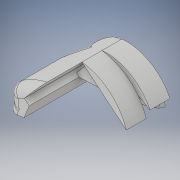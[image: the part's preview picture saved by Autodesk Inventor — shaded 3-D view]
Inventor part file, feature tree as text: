
AUTODESK INVENTOR PART (.ipt)
format: ipt  version: 2017 (Build 210142000, 142)  size: 682,496 bytes
history: native  units: mm
features: sketch x25, extrude x21, fillet x6, plane x5, other x3, boolean_combine x1, revolve x1, sweep x1
ambient origin geometry x8: Origin, YZ Plane, XZ Plane, XY Plane, X Axis, Y Axis, Z Axis, Center Point
bodies: Solid1 (feature_tree), Solid2 (feature_tree), Solid3 (feature_tree), Solid4 (feature_tree), Solid5 (feature_tree)
feature tree (63):
  extrude  "Extrusion1"  Depth=35.0mm
  plane  "Work Plane1"
  extrude  "Extrusion2"  Depth=33.005mm
  extrude  "Extrusion3"  TaperAngle=0.0deg  [1 undecoded]
  plane  "Work Plane2"
  extrude  "Extrusion4"  Depth=20.0mm
  other  "Work Axis1"
  extrude  "Extrusion5"  Depth=10.0mm
  sketch  "Sketch6"  dims[d12=48.556624mm d13=20.0mm d14=0.0mm]
  boolean_combine  "Combine1"
  extrude  "Extrusion6"  Depth=20.0mm TaperAngle=0.0deg
  extrude  "Extrusion7"  Depth=20.0mm TaperAngle=0.0deg
  other  "Work Axis2"
  fillet  "Fillet1"  Radius=53.287466mm
  revolve  "Revolution1"  [1 undecoded]
  extrude  "Extrusion8"  Depth=20.0mm
  sketch  "Sketch10"  dims[d25=7.433428mm d26=13.25mm d27=0.0mm]
  plane  "Work Plane3"
  sweep  "Sweep1"
  extrude  "Extrusion9"  TaperAngle=90.0deg  [1 undecoded]
  fillet  "Fillet2"  Radius=40.197898mm
  extrude  "Extrusion10"  Depth=15.060899mm
  extrude  "Extrusion11"  Depth=10.650813mm
  extrude  "Extrusion12"  Depth=5.3475mm
  fillet  "Fillet3"  Radius=15.0mm
  fillet  "Fillet4"  [1 undecoded]
  fillet  "Fillet5"  Radius=27.295196mm
  other  "Bend Part1"
  extrude  "Extrusion13"  Depth=20.0mm
  plane  "Work Plane4"
  extrude  "Extrusion14"  TaperAngle=0.0deg  [1 undecoded]
  fillet  "Fillet6"  Radius=13.25mm
  extrude  "Extrusion15"  Depth=75.0mm TaperAngle=0.0deg
  plane  "Work Plane5"
  extrude  "Extrusion16"  Depth=10.80569mm
  extrude  "Extrusion17"  Depth=4.8mm TaperAngle=0.0deg
  extrude  "Extrusion18"  Depth=10.0mm
  extrude  "Extrusion19"  Depth=2.0mm TaperAngle=180.0deg
  extrude  "Extrusion20"  Depth=18.153275mm
  extrude  "Extrusion21"  TaperAngle=90.0deg  [1 undecoded]
  sketch  "Sketch1"  dims[d0=60.0mm d1=35.0mm]
  sketch  "Sketch2"  dims[d2=60.0mm d3=33.005mm]
  sketch  "Sketch3"  dims[d4=75.0mm d5=0.0mm d6=0.0mm]
  sketch  "Sketch4"  dims[d7=35.0mm d8=20.0mm]
  sketch  "Sketch5"  dims[d9=55.0mm d10=0.0mm d11=10.0mm]
  sketch  "Sketch7"  dims[d15=90.0deg d16=20.0mm d17=0.0mm d18=53.287466mm]
  sketch  "Sketch8"  dims[d19=20.0mm d20=0.0mm d21=14.476257mm]
  sketch  "Sketch9"  dims[d22=20.0mm d23=0.0mm d24=61.358233mm]
  sketch  "Sketch11"  dims[d28=10.0mm d29=90.0deg d30=40.197898mm]
  sketch  "Sketch12"  dims[d31=90.965929mm d32=15.060899mm]
  sketch  "Sketch13"  dims[d33=0.0mm d34=0.0mm d35=10.650813mm]
  sketch  "Sketch15"  dims[d36=90.0deg d37=5.3475mm d38=15.0mm d39=45.0deg d40=27.295196mm]
  sketch  "Sketch16"  dims[d41=20.0mm d42=5.348mm]
  sketch  "Sketch18"  dims[d43=60.0mm d44=0.0mm d45=0.0mm d46=13.25mm d47=0.0mm]
  sketch  "Sketch19"  dims[d48=10.0mm d49=75.0mm d50=0.0mm]
  sketch  "Sketch20"  dims[d52=10.0mm d53=10.80569mm]
  sketch  "Sketch21"  dims[d54=10.0mm d55=0.0mm d56=4.8mm d57=0.0mm]
  sketch  "Sketch22"  dims[d58=10.0mm d59=10.0mm]
  sketch  "Sketch23"  dims[d60=10.0mm d62=2.0mm d63=180.0deg]
  sketch  "Sketch24"  dims[d64=18.153275mm d65=18.153275mm]
  sketch  "Sketch25"  dims[d66=75.0mm d67=0.0mm d68=90.0deg]
  sketch  "Sketch26"  dims[d69=75.0mm]
  sketch  "Sketch27"  dims[d70=57.396209mm d71=75.0mm d72=0.0mm d73=2.0mm d74=27.7545mm d75=17.5mm d76=5.0mm d77=0.0mm d78=20.0mm d79=28.8585mm d80=10.0mm d81=0.0mm d82=20.0mm d83=3.0mm d85=0.0mm d86=0.0mm d87=10.0mm d88=0.0mm d89=3.357147mm d90=50.0mm d91=0.0mm d92=10.0mm d93=0.0mm d94=19.999532mm d95=2.99993mm d97=13.189012mm d98=19.999532mm d99=2.99993mm d100=0.0mm d101=11.072637mm d102=13.0mm d103=5.0mm d104=0.0mm d105=0.0mm d106=13.0mm d107=0.0mm]
note: 6 required parameter values undecoded (feature->parameter linkage not recoverable at this tier; creation-order binding heuristic only, values carry confidence <= 0.55)